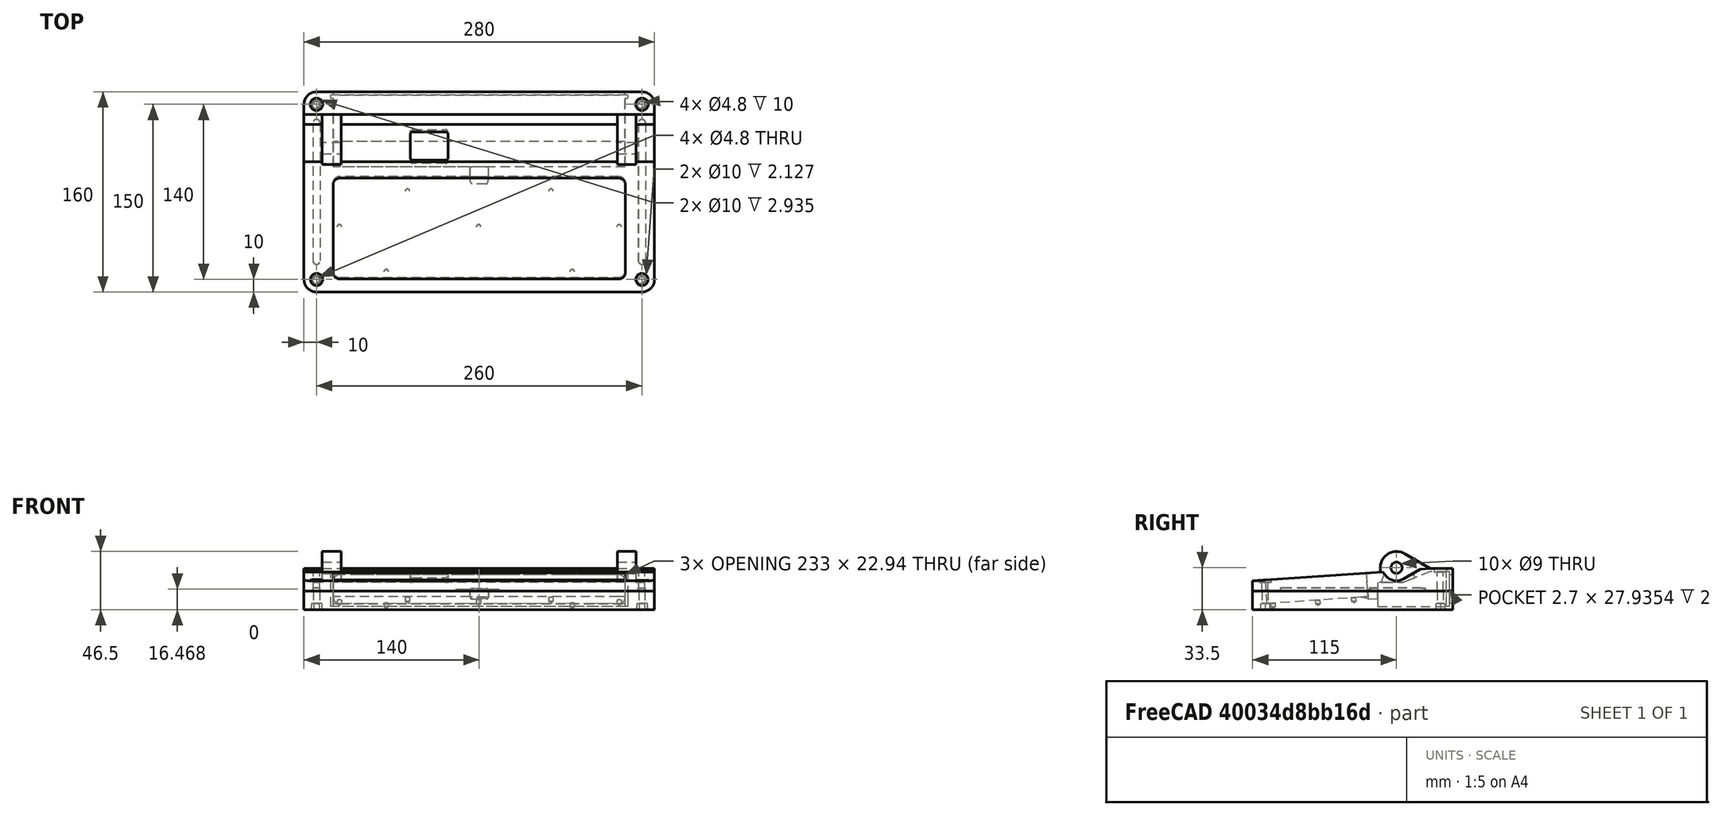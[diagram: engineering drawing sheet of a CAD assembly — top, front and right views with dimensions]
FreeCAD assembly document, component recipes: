
FREECAD ASSEMBLY — COMPONENT RECIPES ("BottomEnclosure_v4")

This assembly document has 8 components, labeled P0..P7 below (a component is one placed body or linked part). 7 of them carry a construction recipe — the FreeCAD feature program that regenerates the part from scratch, quoted from this document or its linked companion documents; the rest are supplied as boundary geometry only. No exploded tour is included for this assembly.
COMPONENT P0 — recipe-attached ("Bottom Enclosure - 1", modeled in this document).
Construction recipe (the document's own serialized feature program — sketch geometry with constraints, then the solid features built on it; lengths are millimeters unless a unit is written):

FEATURE [PartDesign::SubShapeBinder] Binder018
  BindCopyOnChange = 0
  BindMode = 0
  ClaimChildren = false
  Context = -> Body [Binder018.]
  Fuse = false
  MakeFace = false
  OffsetFill = false
  OffsetIntersection = false
  OffsetJoinType = 0
  OffsetOpenResult = false
  PartialLoad = false
  Placement = pos=(2.42e-14,-48.0113,26.6427) rot=(1,0,0;0.069813rad)
  Refine = true
  Relative = true
  Support = -> [Link001,Link002]
  _Version = 2
  expr: .Placement.Rotation.Angle = <<Vars>>.hood_angle
FEATURE [PartDesign::Boolean] Boolean
  Group = -> [Binder019]
  Refine = true
  Suppressed = false
  Type = 0
  UsePlacement = true
FEATURE [PartDesign::SubShapeBinder] Binder020
  BindCopyOnChange = 0
  BindMode = 0
  ClaimChildren = false
  Context = -> Body [Binder020.]
  Fuse = false
  MakeFace = false
  OffsetFill = false
  OffsetIntersection = false
  OffsetJoinType = 0
  OffsetOpenResult = false
  PartialLoad = false
  Placement = pos=(0,0,-19) rot=(0,0,1;0rad)
  Refine = true
  Relative = true
  Support = -> [Binder018]
  _Version = 2
FEATURE [PartDesign::SubShapeBinder] Binder021
  BindCopyOnChange = 0
  BindMode = 0
  ClaimChildren = false
  Context = -> Body [Binder021.]
  Fuse = false
  MakeFace = true
  Offset = 0.2
  OffsetFill = false
  OffsetIntersection = false
  OffsetJoinType = 2
  OffsetOpenResult = false
  PartialLoad = false
  Refine = true
  Relative = true
  Support = -> [Binder020[Edge14,Edge13,Edge7,Edge8,Edge9,Edge10,Edge11,Edge12]]
  _Version = 2
  expr: Offset = <<Vars>>.clearance
FEATURE [PartDesign::Pocket] Pocket005
  BaseFeature = -> Boolean
  Direction = (0,0.0697565,-0.997564)
  Length = 5
  Length2 = 5
  Profile = -> Binder021
  Refine = true
  Reversed = true
  Suppressed = false
  Type = 1
FEATURE [Sketcher::SketchObject] Sketch018  label="Sketch019"
  ArcFitTolerance = 1e-06
  AttachmentSupport = -> [Binder021]
  ExternalGeometry = -> [Pocket005]
  FullyConstrained = true
  MakeInternals = false
  MapMode = 5
  Placement = pos=(0,-0.765452,10.9465) rot=(1,0,0;0.069813rad)
  sketch-geometry (7):
    g0: Circle CenterX=-57.3 CenterY=-18.7812 CenterZ=0 NormalX=0 NormalY=0 NormalZ=1 AngleXU=0 Radius=2.75
    g1: Circle CenterX=-0.5 CenterY=-47.3612 CenterZ=0 NormalX=0 NormalY=0 NormalZ=1 AngleXU=0 Radius=2.75
    g2: Circle CenterX=57.3 CenterY=-18.7812 CenterZ=0 NormalX=0 NormalY=0 NormalZ=1 AngleXU=0 Radius=2.75
    g3: Circle CenterX=111.8 CenterY=-47.3612 CenterZ=0 NormalX=0 NormalY=0 NormalZ=1 AngleXU=0 Radius=2.75
    g4: Circle CenterX=-111.8 CenterY=-47.3612 CenterZ=0 NormalX=0 NormalY=0 NormalZ=1 AngleXU=0 Radius=2.75
    g5: Circle CenterX=-74.3 CenterY=-83.2812 CenterZ=0 NormalX=0 NormalY=0 NormalZ=1 AngleXU=0 Radius=2.75
    g6: Circle CenterX=74.3 CenterY=-83.2812 CenterZ=0 NormalX=0 NormalY=0 NormalZ=1 AngleXU=0 Radius=2.75
  constraints (22):
    c: Equal(g2,g1)
    c: Equal(g1,g0)
    c: Diameter(g1) = 5.5
    c: Equal(g4,g1)
    c: Equal(g1,g3)
    c: Horizontal(g5,g6)
    c: Equal(g6,g5)
    c: Equal(g5,g1)
    c: DistanceY(g5,g0) = 64.5
    c: DistanceX(g5,g0) = 17
    c: DistanceX(g2,g6) = 17
    c: DistanceX(g-3,g4) = 4.9
    c: DistanceY(g4,g-3) = 35.25
    c: DistanceX(g3,g-4) = 4.9
    c: DistanceY(g3,g-4) = 35.25
    c: DistanceX(g-3,g1) = 116.2
    c: DistanceX(g1,g-4) = 117.2
    c: DistanceY(g1,g-3) = 35.25
    c: DistanceX(g2,g-4) = 59.4
    c: DistanceY(g2,g-4) = 6.67
    c: DistanceX(g-3,g0) = 59.4
    c: DistanceY(g0,g-3) = 6.67
FEATURE [PartDesign::SubShapeBinder] Binder023
  BindCopyOnChange = 0
  BindMode = 0
  ClaimChildren = false
  Context = -> Body [Binder023.]
  Fuse = false
  MakeFace = true
  OffsetFill = false
  OffsetIntersection = false
  OffsetJoinType = 0
  OffsetOpenResult = false
  PartialLoad = false
  Refine = true
  Relative = true
  Support = -> [Sketch019]
  _Version = 2
FEATURE [PartDesign::Hole] Hole
  BaseFeature = -> Pocket005
  CustomThreadClearance = 0
  Depth = 3
  DepthType = 0
  Diameter = 3.5
  DrillForDepth = false
  DrillPoint = 1
  DrillPointAngle = 118
  HoleCutCountersinkAngle = 90
  HoleCutCustomValues = false
  HoleCutDepth = 0
  HoleCutDiameter = 6.1
  HoleCutType = 0
  ModelThread = false
  Profile = -> Sketch018
  Refine = true
  Suppressed = false
  Tapered = false
  TaperedAngle = 90
  ThreadClass = 0
  ThreadDepth = 3
  ThreadDepthType = 0
  ThreadDirection = 0
  ThreadFit = 0
  ThreadSize = 0
  ThreadType = 0
  Threaded = false
  UseCustomThreadClearance = false
  expr: Diameter = <<Vars>>.nut_inserts_m2
FEATURE [Sketcher::SketchObject] Sketch019  label="Sketch020"
  ArcFitTolerance = 1e-06
  ExternalGeometry = -> [Hole]
  FullyConstrained = true
  MakeInternals = false
  MapMode = 5
  Placement = pos=(0,-6.89436,-0.482101) rot=(1,0,0;1.64061rad)
  sketch-geometry (12):
    g0: LineSegment StartX=-7.5 StartY=14.9732 StartZ=0 EndX=-7.5 EndY=10.9732 EndZ=0
    g1: LineSegment StartX=-5.5 StartY=8.9732 StartZ=0 EndX=5.5 EndY=8.9732 EndZ=0
    g2: LineSegment StartX=7.5 StartY=10.9732 StartZ=0 EndX=7.5 EndY=14.9732 EndZ=0
    g3: LineSegment StartX=5.5 StartY=16.9732 StartZ=0 EndX=-5.5 EndY=16.9732 EndZ=0
    g4: ArcOfCircle CenterX=-5.5 CenterY=14.9732 CenterZ=0 NormalX=0 NormalY=0 NormalZ=1 AngleXU=0 Radius=2 StartAngle=1.5708 EndAngle=3.14159
    g5: GeomPoint [constr] X=-7.5 Y=16.9732 Z=0
    g6: ArcOfCircle CenterX=5.5 CenterY=14.9732 CenterZ=0 NormalX=0 NormalY=0 NormalZ=1 AngleXU=0 Radius=2 StartAngle=3.45e-14 EndAngle=1.5708
    g7: GeomPoint [constr] X=7.5 Y=16.9732 Z=0
    g8: ArcOfCircle CenterX=-5.5 CenterY=10.9732 CenterZ=0 NormalX=0 NormalY=0 NormalZ=1 AngleXU=0 Radius=2 StartAngle=3.14159 EndAngle=4.71239
    g9: GeomPoint [constr] X=-7.5 Y=8.9732 Z=0
    g10: ArcOfCircle CenterX=5.5 CenterY=10.9732 CenterZ=0 NormalX=0 NormalY=0 NormalZ=1 AngleXU=0 Radius=2 StartAngle=4.71239 EndAngle=6.28319
    g11: GeomPoint [constr] X=7.5 Y=8.9732 Z=0
  constraints (27):
    c: Vertical(g0)
    c: Vertical(g2)
    c: Horizontal(g1)
    c: Symmetric(g5,g7,g-2)
    c: PointOnObject(g5,g0)
    c: PointOnObject(g5,g3)
    c: Tangent(g0,g4) = -1.5708
    c: Tangent(g3,g4) = -1.5708
    c: PointOnObject(g7,g2)
    c: PointOnObject(g7,g3)
    c: Tangent(g2,g6) = -1.5708
    c: Tangent(g3,g6) = -1.5708
    c: Equal(g6,g4)
    c: Radius(g4) = 2
    c: DistanceY(g11,g3) = 8
    c: DistanceX(g0,g2) = 15
    c: PointOnObject(g9,g0)
    c: PointOnObject(g9,g1)
    c: Tangent(g0,g8) = -1.5708
    c: Tangent(g1,g8) = -1.5708
    c: PointOnObject(g11,g1)
    c: PointOnObject(g11,g2)
    c: Tangent(g1,g10) = -1.5708
    c: Tangent(g2,g10) = -1.5708
    c: Equal(g8,g10)
    c: Equal(g10,g6)
    c: DistanceY(g-3,g5) = 6
FEATURE [PartDesign::Pocket] Pocket006
  BaseFeature = -> Hole
  Direction = (0,-0.997564,-0.0697565)
  Length = 5
  Length2 = 5
  Profile = -> Binder023
  Refine = true
  Reversed = true
  Suppressed = false
  Type = 2
FEATURE [PartDesign::SubShapeBinder] Binder054
  BindCopyOnChange = 0
  BindMode = 0
  ClaimChildren = false
  Context = -> Body [Binder054.]
  Fuse = false
  MakeFace = true
  OffsetFill = false
  OffsetIntersection = false
  OffsetJoinType = 0
  OffsetOpenResult = false
  PartialLoad = false
  Refine = true
  Relative = true
  Support = -> [Sketch019]
  _Version = 2
FEATURE [PartDesign::Pocket] Pocket020
  BaseFeature = -> Pocket006
  Direction = (0,-1,0.25)
  Length = 20
  Length2 = 5
  Profile = -> Binder054
  Refine = true
  Suppressed = false
  Type = 0
  UseCustomVector = true
FEATURE [PartDesign::Body] Body  label="Bottom Enclosure - 1"
  AllowCompound = false
  Group = -> [Binder018,Boolean,Binder020,Binder021,Pocket005,Hole,Sketch018,Sketch019,Binder023,Pocket006,Binder054,Pocket020]
  Origin = -> Origin
  Tip = -> Pocket020
COMPONENT P1 — recipe-attached ("Bottom Enclosure - Base", modeled in this document).
Construction recipe (the document's own serialized feature program — sketch geometry with constraints, then the solid features built on it; lengths are millimeters unless a unit is written):

FEATURE [Sketcher::SketchObject] Sketch008
  ArcFitTolerance = 1e-06
  AttachmentSupport = -> [YZ_Plane002]
  FullyConstrained = true
  MakeInternals = false
  MapMode = 5
  Placement = pos=(0,0,0) rot=(0.57735,0.57735,0.57735;2.0944rad)
  expr: Constraints[15] = <<Vars>>.hood_angle
  expr: Constraints[16] = <<Vars>>.bottom_enclosure_height
  expr: Constraints[8] = <<Vars>>.top_enclosure_height
  expr: Constraints[9] = <<Vars>>.bottom_enclosure_depth
  sketch-geometry (12):
    g0: LineSegment StartX=-100 StartY=0 StartZ=0 EndX=-100 EndY=23.0073 EndZ=0
    g1: LineSegment StartX=-100 StartY=23.0073 StartZ=0 EndX=0 EndY=30 EndZ=0
    g2: LineSegment StartX=60 StartY=32.9354 StartZ=0 EndX=60 EndY=0 EndZ=0
    g3: LineSegment StartX=60 StartY=0 StartZ=0 EndX=-100 EndY=0 EndZ=0
    g4: LineSegment [constr] StartX=0 StartY=30 StartZ=0 EndX=-100 EndY=30 EndZ=0
    g5: LineSegment [constr] StartX=-100 StartY=30 StartZ=0 EndX=-100 EndY=23.0073 EndZ=0
    g6: LineSegment [constr] StartX=41.9779 StartY=32.9354 StartZ=0 EndX=21.5 EndY=44.7583 EndZ=0
    g7: LineSegment StartX=0 StartY=30 StartZ=0 EndX=41.9779 EndY=32.9354 EndZ=0
    g8: LineSegment StartX=41.9779 StartY=32.9354 StartZ=0 EndX=60 EndY=32.9354 EndZ=0
    g9: Circle CenterX=15 CenterY=33.5 CenterZ=0 NormalX=0 NormalY=0 NormalZ=1 AngleXU=0 Radius=4.5
    g10: Circle CenterX=15 CenterY=33.5 CenterZ=0 NormalX=0 NormalY=0 NormalZ=1 AngleXU=0 Radius=10
    g11: LineSegment [constr] StartX=15 StartY=33.5 StartZ=0 EndX=21.5 EndY=44.7583 EndZ=0
  constraints (33):
    c: PointOnObject(g0,g-1)
    c: Vertical(g0)
    c: Coincident(g0,g1)
    c: PointOnObject(g1,g-2)
    c: PointOnObject(g2,g-1)
    c: Vertical(g2)
    c: Coincident(g2,g3)
    c: Coincident(g3,g0)
    c: DistanceX(g0,g-1) = 100
    c: DistanceY(g0,g1) = 30
    c: Coincident(g1,g4)
    c: Horizontal(g4)
    c: Coincident(g4,g5)
    c: Coincident(g5,g0)
    c: Vertical(g5)
    c: Angle(g4,g1) = 0.0698132
    c: DistanceX(g0,g2) = 160
    c: Angle(g6,g-1) = 0.523599
    c: Coincident(g7,g1)
    c: Coincident(g7,g6)
    c: Coincident(g8,g6)
    c: Coincident(g8,g2)
    c: Horizontal(g8)
    c: Parallel(g1,g7)
    c: DistanceX(g-1,g9) = 15
    c: Diameter(g9) = 9
    c: DistanceY(g-1,g9) = 33.5
    c: Coincident(g10,g9)
    c: Diameter(g10) = 20
    c: Coincident(g11,g9)
    c: Coincident(g6,g11)
    c: Perpendicular(g6,g11)
    c: Distance(g11) = 13
FEATURE [Sketcher::SketchObject] Sketch
  ArcFitTolerance = 1e-06
  AttachmentSupport = -> [YZ_Plane002]
  ExternalGeometry = -> [Sketch008]
  FullyConstrained = true
  MakeInternals = false
  MapMode = 5
  Placement = pos=(0,0,0) rot=(0.57735,0.57735,0.57735;2.0944rad)
  sketch-geometry (6):
    g0: ArcOfCircle CenterX=15 CenterY=33.5 CenterZ=0 NormalX=0 NormalY=0 NormalZ=1 AngleXU=0 Radius=10.5 StartAngle=3.83972 EndAngle=5.23599
    g1: LineSegment StartX=3.99563 StartY=30.2794 StartZ=0 EndX=6.95653 EndY=26.7507 EndZ=0
    g2: LineSegment StartX=20.25 StartY=24.4067 StartZ=0 EndX=34.0635 EndY=32.382 EndZ=0
    g3: LineSegment [constr] StartX=6.95653 StartY=26.7507 StartZ=0 EndX=7.33956 EndY=27.0721 EndZ=0
    g4: LineSegment [constr] StartX=7.33956 StartY=27.0721 StartZ=0 EndX=15 EndY=33.5 EndZ=0
    g5: LineSegment StartX=3.99563 StartY=30.2794 StartZ=0 EndX=34.0635 EndY=32.382 EndZ=0
  constraints (15):
    c: Coincident(g0,g-3)
    c: PointOnObject(g1,g-5)
    c: Coincident(g3,g1)
    c: Coincident(g4,g0)
    c: PointOnObject(g2,g-5)
    c: Angle(g-1,g2) = 0.523599
    c: Tangent(g0,g1) = -1.5708
    c: Tangent(g0,g2) = -1.5708
    c: Coincident(g3,g4)
    c: PointOnObject(g3,g-4)
    c: Parallel(g3,g4)
    c: Coincident(g5,g1)
    c: Coincident(g5,g2)
    c: Angle(g-1,g4) = 0.698132
    c: Distance(g0,g3) = 0.5
FEATURE [Sketcher::SketchObject] Sketch012  label="Sketch013"
  ArcFitTolerance = 1e-06
  AttachmentSupport = -> [YZ_Plane002]
  ExternalGeometry = -> [Sketch,Sketch008]
  FullyConstrained = true
  MakeInternals = false
  MapMode = 5
  Placement = pos=(0,0,0) rot=(0.57735,0.57735,0.57735;2.0944rad)
  sketch-geometry (7):
    g0: ArcOfCircle CenterX=15 CenterY=33.5 CenterZ=0 NormalX=0 NormalY=0 NormalZ=1 AngleXU=0 Radius=13 StartAngle=1.0472 EndAngle=3.40062
    g1: LineSegment StartX=21.5 StartY=44.7583 StartZ=0 EndX=41.9779 EndY=32.9354 EndZ=0
    g2: LineSegment StartX=2.43368 StartY=30.1702 StartZ=0 EndX=3.99563 EndY=30.2794 EndZ=0
    g3: LineSegment StartX=34.0635 StartY=32.382 StartZ=0 EndX=41.9779 EndY=32.9354 EndZ=0
    g4: LineSegment StartX=3.99563 StartY=30.2794 StartZ=0 EndX=6.95653 EndY=26.7507 EndZ=0
    g5: LineSegment StartX=20.25 StartY=24.4067 StartZ=0 EndX=34.0635 EndY=32.382 EndZ=0
    g6: ArcOfCircle CenterX=15 CenterY=33.5 CenterZ=0 NormalX=0 NormalY=0 NormalZ=1 AngleXU=0 Radius=10.5 StartAngle=3.83972 EndAngle=5.23599
  constraints (16):
    c: Diameter(g0) = 26
    c: Coincident(g0,g-3)
    c: Coincident(g1,g-6)
    c: Tangent(g0,g1) = 1.5708
    c: PointOnObject(g0,g-6)
    c: Coincident(g2,g0)
    c: Coincident(g2,g-4)
    c: Coincident(g3,g-5)
    c: Coincident(g3,g1)
    c: Coincident(g4,g2)
    c: Coincident(g4,g-4)
    c: Coincident(g5,g-5)
    c: Coincident(g5,g3)
    c: Coincident(g6,g4)
    c: Coincident(g6,g5)
    c: Tangent(g6,g-3)
FEATURE [Sketcher::SketchObject] Sketch013  label="Sketch014"
  ArcFitTolerance = 1e-06
  AttachmentSupport = -> [XY_Plane002]
  FullyConstrained = true
  MakeInternals = false
  MapMode = 5
  expr: Constraints[10] = <<Vars>>.wire_hole_offset_x
  expr: Constraints[9] = <<Vars>>.wire_hole_width
  sketch-geometry (5):
    g0: LineSegment StartX=-55 StartY=5 StartZ=0 EndX=-25 EndY=5 EndZ=0
    g1: LineSegment StartX=-25 StartY=5 StartZ=0 EndX=-25 EndY=25 EndZ=0
    g2: LineSegment StartX=-25 StartY=25 StartZ=0 EndX=-55 EndY=25 EndZ=0
    g3: LineSegment StartX=-55 StartY=25 StartZ=0 EndX=-55 EndY=5 EndZ=0
    g4: GeomPoint [constr] X=-40 Y=15 Z=0
  constraints (13):
    c: Coincident(g0,g1)
    c: Coincident(g1,g2)
    c: Coincident(g2,g3)
    c: Coincident(g3,g0)
    c: Horizontal(g0)
    c: Horizontal(g2)
    c: Vertical(g1)
    c: Vertical(g3)
    c: Symmetric(g2,g0,g4)
    c: DistanceX(g2,g2) = 30
    c: DistanceX(g4,g-1) = 40
    c: DistanceY(g-1,g4) = 15
    c: DistanceY(g3,g3) = 20
FEATURE [PartDesign::SubShapeBinder] Binder014
  BindCopyOnChange = 0
  BindMode = 0
  ClaimChildren = false
  Context = -> Body002 [Binder014.]
  Fuse = false
  MakeFace = true
  OffsetFill = false
  OffsetIntersection = false
  OffsetJoinType = 0
  OffsetOpenResult = false
  PartialLoad = false
  Refine = true
  Relative = true
  Support = -> [Sketch008[Edge2,Edge3,Edge4,Edge5,Edge6,Edge1]]
  _Version = 2
FEATURE [PartDesign::Pad] Pad001
  Direction = (1,0,0)
  Length = 280
  Length2 = 10
  Midplane = true
  Profile = -> Binder014
  Refine = true
  Suppressed = false
  Type = 0
  expr: Length = <<Vars>>.top_enclosure_width
FEATURE [Sketcher::SketchObject] Sketch014  label="Sketch015"
  ArcFitTolerance = 1e-06
  AttachmentSupport = -> [YZ_Plane002]
  FullyConstrained = true
  MakeInternals = false
  MapMode = 5
  Placement = pos=(0,0,0) rot=(0.57735,0.57735,0.57735;2.0944rad)
FEATURE [PartDesign::Pocket] Pocket
  BaseFeature = -> Pad001
  Direction = (-1,0,0)
  Length = 5
  Length2 = 5
  Midplane = true
  Profile = -> Sketch
  ReferenceAxis = -> Sketch [N_Axis]
  Refine = true
  Suppressed = false
  Type = 1
FEATURE [PartDesign::SubShapeBinder] Binder
  BindCopyOnChange = 0
  BindMode = 0
  ClaimChildren = false
  Context = -> Body002 [Binder.]
  Fuse = false
  MakeFace = true
  OffsetFill = false
  OffsetIntersection = false
  OffsetJoinType = 0
  OffsetOpenResult = false
  PartialLoad = false
  Placement = pos=(110.4,0,0) rot=(0,0,1;0rad)
  Refine = true
  Relative = true
  Support = -> [Sketch012]
  _Version = 2
  expr: .Placement.Base.x = (<<Vars>>.top_enclosure_width - 32 * 2) / 2 + 2.4
FEATURE [PartDesign::Pad] Pad
  BaseFeature = -> Pocket
  Direction = (1,0,0)
  Length = 15
  Length2 = 10
  Profile = -> Binder
  Refine = true
  Suppressed = false
  Type = 0
FEATURE [PartDesign::Mirrored] Mirrored
  BaseFeature = -> Pad
  MirrorPlane = -> YZ_Plane002
  Originals = -> [Pad]
  Refine = true
  Suppressed = false
  TransformMode = 0
FEATURE [PartDesign::SubShapeBinder] Binder015
  BindCopyOnChange = 0
  BindMode = 0
  ClaimChildren = false
  Context = -> Body002 [Binder015.]
  Fuse = false
  MakeFace = true
  OffsetFill = false
  OffsetIntersection = false
  OffsetJoinType = 0
  OffsetOpenResult = false
  PartialLoad = false
  Refine = true
  Relative = true
  Support = -> [Sketch008[Edge7]]
  _Version = 2
FEATURE [PartDesign::Pocket] Pocket001
  BaseFeature = -> Mirrored
  Direction = (-1,0,0)
  Length = 5
  Length2 = 5
  Midplane = true
  Profile = -> Binder015
  Refine = true
  Suppressed = false
  Type = 1
FEATURE [Sketcher::SketchObject] Sketch015  label="Sketch016"
  ArcFitTolerance = 1e-06
  AttachmentSupport = -> [YZ_Plane002]
  ExternalGeometry = -> [Pocket001]
  FullyConstrained = true
  MakeInternals = false
  MapMode = 5
  Placement = pos=(0,0,0) rot=(0.57735,0.57735,0.57735;2.0944rad)
  expr: Constraints[10] = <<Vars>>.wall
  expr: Constraints[13] = <<Vars>>.wall
  expr: Constraints[17] = <<Vars>>.wall
  expr: Constraints[9] = <<Vars>>.wall
  sketch-geometry (6):
    g0: LineSegment StartX=0 StartY=21.9067 StartZ=0 EndX=0 EndY=2.5 EndZ=0
    g1: LineSegment StartX=0 StartY=2.5 StartZ=0 EndX=57.5 EndY=2.5 EndZ=0
    g2: LineSegment StartX=57.5 StartY=2.5 StartZ=0 EndX=57.5 EndY=30.4354 EndZ=0
    g3: LineSegment StartX=20.25 StartY=21.9067 StartZ=0 EndX=0 EndY=21.9067 EndZ=0
    g4: LineSegment StartX=57.5 StartY=30.4354 StartZ=0 EndX=41.9779 EndY=30.4354 EndZ=0
    g5: LineSegment StartX=41.9779 StartY=30.4354 StartZ=0 EndX=20.25 EndY=21.9067 EndZ=0
  constraints (18):
    c: Coincident(g0,g1)
    c: Coincident(g1,g2)
    c: Coincident(g2,g4)
    c: Coincident(g3,g0)
    c: Vertical(g0)
    c: Vertical(g2)
    c: Horizontal(g1)
    c: Coincident(g5,g3)
    c: Coincident(g4,g5)
    c: DistanceX(g2,g-7) = 2.5
    c: DistanceY(g2,g-7) = 2.5
    c: Horizontal(g4)
    c: PointOnObject(g0,g-2)
    c: DistanceY(g-8,g1) = 2.5
    c: Vertical(g4,g-6)
    c: Vertical(g3,g-5)
    c: Horizontal(g3)
    c: DistanceY(g3,g-5) = 2.5
FEATURE [PartDesign::SubShapeBinder] Binder016
  BindCopyOnChange = 0
  BindMode = 0
  ClaimChildren = false
  Context = -> Body002 [Binder016.]
  Fuse = false
  MakeFace = true
  OffsetFill = false
  OffsetIntersection = false
  OffsetJoinType = 0
  OffsetOpenResult = false
  PartialLoad = false
  Refine = true
  Relative = true
  Support = -> [Sketch015]
  _Version = 2
FEATURE [PartDesign::Pocket] Pocket002
  BaseFeature = -> Pocket001
  Direction = (-1,0,0)
  Length = 233
  Length2 = 5
  Midplane = true
  Profile = -> Binder016
  Refine = true
  Suppressed = false
  Type = 0
  expr: Length = <<Vars>>.keyboard_plate_width
FEATURE [PartDesign::Fillet] Fillet
  Base = -> Pocket002 [Edge25,Edge26,Edge27,Edge33]
  BaseFeature = -> Pocket002
  Radius = 10
  Refine = true
  SupportTransform = false
  Suppressed = false
  UseAllEdges = false
  expr: Radius = <<Vars>>.ext_radius
FEATURE [Sketcher::SketchObject] Sketch016  label="Sketch017"
  ArcFitTolerance = 1e-06
  AttachmentSupport = -> [Fillet]
  ExternalGeometry = -> [Fillet]
  FullyConstrained = true
  MakeInternals = false
  MapMode = 5
  Placement = pos=(0,60,0) rot=(0,0.707107,0.707107;3.14159rad)
  expr: Constraints[27] = <<Vars>>.ext_radius / 2
  expr: Constraints[6] = <<Vars>>.wall
  expr: Constraints[7] = <<Vars>>.wall
  sketch-geometry (12):
    g0: LineSegment StartX=-116.5 StartY=22.9354 StartZ=0 EndX=-116.5 EndY=10 EndZ=0
    g1: LineSegment StartX=-111.5 StartY=5 StartZ=0 EndX=111.5 EndY=5 EndZ=0
    g2: LineSegment StartX=116.5 StartY=10 StartZ=0 EndX=116.5 EndY=22.9354 EndZ=0
    g3: LineSegment StartX=111.5 StartY=27.9354 StartZ=0 EndX=-111.5 EndY=27.9354 EndZ=0
    g4: ArcOfCircle CenterX=111.5 CenterY=22.9354 CenterZ=0 NormalX=0 NormalY=0 NormalZ=1 AngleXU=0 Radius=5 StartAngle=0 EndAngle=1.5708
    g5: GeomPoint [constr] X=116.5 Y=27.9354 Z=0
    g6: ArcOfCircle CenterX=111.5 CenterY=10 CenterZ=0 NormalX=0 NormalY=0 NormalZ=1 AngleXU=0 Radius=5 StartAngle=4.71239 EndAngle=6.28319
    g7: GeomPoint [constr] X=116.5 Y=5 Z=0
    g8: ArcOfCircle CenterX=-111.5 CenterY=22.9354 CenterZ=0 NormalX=0 NormalY=0 NormalZ=1 AngleXU=0 Radius=5 StartAngle=1.5708 EndAngle=3.14159
    g9: GeomPoint [constr] X=-116.5 Y=27.9354 Z=0
    g10: ArcOfCircle CenterX=-111.5 CenterY=10 CenterZ=0 NormalX=0 NormalY=0 NormalZ=1 AngleXU=0 Radius=5 StartAngle=3.14159 EndAngle=4.71239
    g11: GeomPoint [constr] X=-116.5 Y=5 Z=0
  constraints (28):
    c: Vertical(g0)
    c: Vertical(g2)
    c: Horizontal(g1)
    c: Horizontal(g3)
    c: PointOnObject(g9,g-3)
    c: PointOnObject(g7,g-4)
    c: DistanceY(g-4,g7) = 2.5
    c: DistanceY(g5,g-4) = 2.5
    c: PointOnObject(g5,g2)
    c: PointOnObject(g5,g3)
    c: Tangent(g2,g4) = -1.5708
    c: Tangent(g3,g4) = -1.5708
    c: PointOnObject(g7,g1)
    c: PointOnObject(g7,g2)
    c: Tangent(g1,g6) = -1.5708
    c: Tangent(g2,g6) = -1.5708
    c: PointOnObject(g9,g0)
    c: PointOnObject(g9,g3)
    c: Tangent(g0,g8) = -1.5708
    c: Tangent(g3,g8) = -1.5708
    c: PointOnObject(g11,g0)
    c: PointOnObject(g11,g1)
    c: Tangent(g0,g10) = -1.5708
    c: Tangent(g1,g10) = -1.5708
    c: Equal(g6,g4)
    c: Equal(g4,g8)
    c: Equal(g8,g10)
    c: Radius(g10) = 5
FEATURE [PartDesign::Pocket] Pocket003
  BaseFeature = -> Fillet
  Direction = (0,-1,2e-16)
  Length = 5
  Length2 = 5
  Profile = -> Sketch016
  ReferenceAxis = -> Sketch016 [N_Axis]
  Refine = true
  Suppressed = false
  Type = 2
FEATURE [Sketcher::SketchObject] Sketch017  label="Sketch018"
  ArcFitTolerance = 1e-06
  AttachmentSupport = -> [Pocket002]
  ExternalGeometry = -> [Pocket002]
  FullyConstrained = true
  MakeInternals = false
  MapMode = 5
  Placement = pos=(0,60,0) rot=(0,0.707107,0.707107;3.14159rad)
  sketch-geometry (4):
    g0: LineSegment StartX=-118.5 StartY=30.4354 StartZ=0 EndX=-118.5 EndY=2.5 EndZ=0
    g1: LineSegment StartX=-118.5 StartY=2.5 StartZ=0 EndX=118.5 EndY=2.5 EndZ=0
    g2: LineSegment StartX=118.5 StartY=2.5 StartZ=0 EndX=118.5 EndY=30.4354 EndZ=0
    g3: LineSegment StartX=118.5 StartY=30.4354 StartZ=0 EndX=-118.5 EndY=30.4354 EndZ=0
  constraints (12):
    c: Coincident(g0,g1)
    c: Coincident(g1,g2)
    c: Coincident(g2,g3)
    c: Coincident(g3,g0)
    c: Vertical(g0)
    c: Vertical(g2)
    c: Horizontal(g1)
    c: Horizontal(g3)
    c: PointOnObject(g-3,g3)
    c: PointOnObject(g-3,g1)
    c: DistanceX(g-4,g2) = 2
    c: DistanceX(g0,g-3) = 2
FEATURE [PartDesign::SubShapeBinder] Binder017
  BindCopyOnChange = 0
  BindMode = 0
  ClaimChildren = false
  Context = -> Body002 [Binder017.]
  Fuse = false
  MakeFace = true
  OffsetFill = false
  OffsetIntersection = false
  OffsetJoinType = 0
  OffsetOpenResult = false
  PartialLoad = false
  Placement = pos=(0,-2.5,0) rot=(0,0,1;0rad)
  Refine = true
  Relative = true
  Support = -> [Sketch017]
  _Version = 2
  expr: .Placement.Base.y = -<<Vars>>.wall
FEATURE [PartDesign::Pocket] Pocket004
  BaseFeature = -> Pocket003
  Direction = (0,-1,3e-16)
  Length = 2.7
  Length2 = 5
  Profile = -> Binder017
  Refine = true
  Suppressed = false
  Type = 0
  expr: Length = <<Vars>>.wall + <<Vars>>.clearance
FEATURE [PartDesign::Body] Body002  label="Bottom Enclosure - Base"
  AllowCompound = false
  Group = -> [Sketch008,Sketch,Sketch012,Binder014,Pad001,Sketch013,Sketch014,Pocket,Binder,Pad,Mirrored,Binder015,Pocket001,Sketch015,Binder016,Pocket002,Fillet,Sketch016,Pocket003,Sketch017,Binder017,Pocket004]
  Origin = -> Origin002
  Tip = -> Pocket004
COMPONENT P2 — recipe-attached ("Bottom Enclosure - 2", modeled in this document).
Construction recipe (the document's own serialized feature program — sketch geometry with constraints, then the solid features built on it; lengths are millimeters unless a unit is written):

FEATURE [PartDesign::Boolean] Boolean001
  Group = -> [Binder025]
  Refine = true
  Suppressed = false
  Type = 0
  UsePlacement = true
FEATURE [Sketcher::SketchObject] Sketch022  label="Sketch023"
  ArcFitTolerance = 1e-06
  AttachmentSupport = -> [YZ_Plane003]
  ExternalGeometry = -> [Boolean001]
  FullyConstrained = true
  MakeInternals = false
  MapMode = 5
  Placement = pos=(0,0,0) rot=(0.57735,0.57735,0.57735;2.0944rad)
  sketch-geometry (5):
    g0: LineSegment StartX=2 StartY=19.9067 StartZ=0 EndX=7.37275 EndY=33.2121 EndZ=0
    g1: LineSegment StartX=25.5013 StartY=33.2121 StartZ=0 EndX=33.1831 EndY=19.9067 EndZ=0
    g2: LineSegment StartX=33.1831 StartY=19.9067 StartZ=0 EndX=2 EndY=19.9067 EndZ=0
    g3: GeomPoint X=5.47608 Y=28.5151 Z=0
    g4: LineSegment StartX=7.37275 StartY=33.2121 StartZ=0 EndX=25.5013 EndY=33.2121 EndZ=0
  constraints (13):
    c: Perpendicular(g-5,g1)
    c: Distance(g1,g-5) = 5
    c: Distance(g-5,g1) = 7
    c: DistanceY(g1,g-4) = 2
    c: Coincident(g2,g1)
    c: Horizontal(g2)
    c: Coincident(g0,g2)
    c: Horizontal(g0,g1)
    c: DistanceX(g-4,g0) = 2
    c: PointOnObject(g3,g0)
    c: Symmetric(g-6,g-6,g3)
    c: Coincident(g4,g0)
    c: Coincident(g4,g1)
FEATURE [PartDesign::SubShapeBinder] Binder029
  BindCopyOnChange = 0
  BindMode = 0
  ClaimChildren = false
  Context = -> Body003 [Binder029.]
  Fuse = false
  MakeFace = true
  OffsetFill = false
  OffsetIntersection = false
  OffsetJoinType = 0
  OffsetOpenResult = false
  PartialLoad = false
  Placement = pos=(-40,0,0) rot=(0,0,1;0rad)
  Refine = true
  Relative = true
  Support = -> [Sketch022]
  _Version = 2
  expr: .Placement.Base.x = -<<Vars>>.wire_hole_offset_x
FEATURE [PartDesign::Pocket] Pocket008
  BaseFeature = -> Boolean001
  Direction = (-1,0,0)
  Length = 30
  Length2 = 5
  Midplane = true
  Profile = -> Binder029
  Refine = true
  Suppressed = false
  Type = 0
  expr: Length = <<Vars>>.wire_hole_width
FEATURE [PartDesign::Fillet] Fillet001
  Base = -> Pocket008 [Edge53,Edge58,Edge57,Edge63]
  BaseFeature = -> Pocket008
  Radius = 2
  Refine = true
  SupportTransform = false
  Suppressed = false
  UseAllEdges = false
FEATURE [PartDesign::Body] Body003  label="Bottom Enclosure - 2"
  AllowCompound = false
  Group = -> [Boolean001,Sketch022,Binder029,Pocket008,Fillet001]
  Origin = -> Origin003
  Tip = -> Fillet001
COMPONENT P3 — recipe-attached ("Bottom Enclosure - 3", modeled in this document).
Construction recipe (the document's own serialized feature program — sketch geometry with constraints, then the solid features built on it; lengths are millimeters unless a unit is written):

FEATURE [PartDesign::Boolean] Boolean002
  Group = -> [Binder030]
  Refine = true
  Suppressed = false
  Type = 0
  UsePlacement = true
FEATURE [PartDesign::Body] Body005  label="Bottom Enclosure - 3"
  AllowCompound = false
  Group = -> [Boolean002]
  Origin = -> Origin005
  Tip = -> Boolean002
COMPONENT P4 — recipe-attached ("Bottom Enclosure - Bottom - 1", modeled in this document).
Construction recipe (the document's own serialized feature program — sketch geometry with constraints, then the solid features built on it; lengths are millimeters unless a unit is written):

FEATURE [PartDesign::Boolean] Boolean003
  Group = -> [Binder031]
  Refine = true
  Suppressed = false
  Type = 0
  UsePlacement = true
FEATURE [PartDesign::SubShapeBinder] Binder050
  BindCopyOnChange = 0
  BindMode = 0
  ClaimChildren = false
  Context = -> Body006 [Binder050.]
  Fuse = false
  MakeFace = true
  Offset = -0.2
  OffsetFill = false
  OffsetIntersection = false
  OffsetJoinType = 2
  OffsetOpenResult = false
  PartialLoad = false
  Placement = pos=(0,0,15) rot=(0,0,1;0rad)
  Refine = true
  Relative = true
  Support = -> [Sketch028[Edge4,Edge6,Edge5,Edge3]]
  _Version = 2
  expr: .Placement.Base.z = <<LocalVars>>.SplitHeight
  expr: Offset = -<<Vars>>.clearance
FEATURE [PartDesign::SubShapeBinder] Binder051
  BindCopyOnChange = 0
  BindMode = 0
  ClaimChildren = false
  Context = -> Body006 [Binder051.]
  Fuse = false
  MakeFace = true
  OffsetFill = false
  OffsetIntersection = false
  OffsetJoinType = 0
  OffsetOpenResult = false
  PartialLoad = false
  Placement = pos=(0,0,15) rot=(0,0,1;0rad)
  Refine = true
  Relative = true
  Support = -> [Sketch028[Edge2,Edge1]]
  _Version = 2
  expr: .Placement.Base.z = <<LocalVars>>.SplitHeight
FEATURE [PartDesign::Pad] Pad002
  BaseFeature = -> Boolean003
  Direction = (0,0,1)
  Length = 2
  Length2 = 10
  Profile = -> Binder050
  Refine = true
  Suppressed = false
  Type = 0
FEATURE [PartDesign::Hole] Hole007
  BaseFeature = -> Pad002
  CustomThreadClearance = 0
  Depth = 652.335
  DepthType = 1
  Diameter = 4.8
  DrillForDepth = false
  DrillPoint = 1
  DrillPointAngle = 118
  HoleCutCountersinkAngle = 90
  HoleCutCustomValues = false
  HoleCutDepth = 0
  HoleCutDiameter = 6.1
  HoleCutType = 0
  ModelThread = false
  Profile = -> Binder051
  Refine = true
  Suppressed = false
  Tapered = false
  TaperedAngle = 90
  ThreadClass = 0
  ThreadDepth = 652.335
  ThreadDepthType = 0
  ThreadDirection = 0
  ThreadFit = 2
  ThreadSize = 11
  ThreadType = 1
  Threaded = false
  UseCustomThreadClearance = false
FEATURE [Sketcher::SketchObject] Sketch029
  ArcFitTolerance = 1e-06
  AttachmentOffset = pos=(0,0,5) rot=(0,0,1;0rad)
  AttachmentSupport = -> [XY_Plane006]
  ExternalGeometry = -> [Binder051]
  FullyConstrained = true
  MakeInternals = false
  MapMode = 5
  Placement = pos=(0,0,5) rot=(0,0,1;0rad)
  sketch-geometry (14):
    g0: LineSegment StartX=-125.959 StartY=50 StartZ=0 EndX=-127.979 EndY=53.5 EndZ=0
    g1: LineSegment StartX=-127.979 StartY=53.5 StartZ=0 EndX=-132.021 EndY=53.5 EndZ=0
    g2: LineSegment StartX=-132.021 StartY=53.5 StartZ=0 EndX=-134.041 EndY=50 EndZ=0
    g3: LineSegment StartX=-134.041 StartY=50 StartZ=0 EndX=-132.021 EndY=46.5 EndZ=0
    g4: LineSegment StartX=-132.021 StartY=46.5 StartZ=0 EndX=-127.979 EndY=46.5 EndZ=0
    g5: LineSegment StartX=-127.979 StartY=46.5 StartZ=0 EndX=-125.959 EndY=50 EndZ=0
    g6: Circle [constr] CenterX=-130 CenterY=50 CenterZ=0 NormalX=0 NormalY=0 NormalZ=1 AngleXU=0 Radius=4.04145
    g7: LineSegment StartX=-125.959 StartY=-90 StartZ=0 EndX=-127.979 EndY=-86.5 EndZ=0
    g8: LineSegment StartX=-127.979 StartY=-86.5 StartZ=0 EndX=-132.021 EndY=-86.5 EndZ=0
    g9: LineSegment StartX=-132.021 StartY=-86.5 StartZ=0 EndX=-134.041 EndY=-90 EndZ=0
    g10: LineSegment StartX=-134.041 StartY=-90 StartZ=0 EndX=-132.021 EndY=-93.5 EndZ=0
    g11: LineSegment StartX=-132.021 StartY=-93.5 StartZ=0 EndX=-127.979 EndY=-93.5 EndZ=0
    g12: LineSegment StartX=-127.979 StartY=-93.5 StartZ=0 EndX=-125.959 EndY=-90 EndZ=0
    g13: Circle [constr] CenterX=-130 CenterY=-90 CenterZ=0 NormalX=0 NormalY=0 NormalZ=1 AngleXU=0 Radius=4.04145
  constraints (32):
    c: Coincident(g0,g1)
    c: Coincident(g1,g2)
    c: Coincident(g2,g3)
    c: Coincident(g3,g4)
    c: Coincident(g4,g5)
    c: Coincident(g5,g0)
    c: Equal(g0, g1-g5) x5
    c: PointOnObject(g0,g6)
    c: PointOnObject(g1,g6)
    c: PointOnObject(g2,g6)
    c: PointOnObject(g3,g6)
    c: PointOnObject(g4,g6)
    c: PointOnObject(g5,g6)
    c: Coincident(g6,g-3)
    c: Coincident(g7,g8)
    c: Coincident(g8,g9)
    c: Coincident(g9,g10)
    c: Coincident(g10,g11)
    c: Coincident(g11,g12)
    c: Coincident(g12,g7)
    c: Equal(g7, g8-g12) x5
    c: PointOnObject(g7,g13)
    c: PointOnObject(g8,g13)
    c: PointOnObject(g9,g13)
    c: PointOnObject(g10,g13)
    c: PointOnObject(g11,g13)
    c: PointOnObject(g12,g13)
    c: Coincident(g13,g-4)
    c: Horizontal(g8)
    c: Horizontal(g1)
    c: DistanceY(g4,g0) = 7
    c: Equal(g6,g13)
FEATURE [PartDesign::Pocket] Pocket016
  BaseFeature = -> Hole007
  Direction = (0,0,-1)
  Length = 5
  Length2 = 5
  Profile = -> Sketch029
  ReferenceAxis = -> Sketch029 [N_Axis]
  Refine = true
  Suppressed = false
  TaperAngle = 4
  Type = 0
FEATURE [PartDesign::Mirrored] Mirrored007
  BaseFeature = -> Pocket016
  MirrorPlane = -> YZ_Plane006
  Originals = -> [Pad002,Hole007,Pocket016]
  Refine = true
  Suppressed = false
  TransformMode = 0
FEATURE [PartDesign::Body] Body006  label="Bottom Enclosure - Bottom - 1"
  AllowCompound = false
  Group = -> [Boolean003,Binder050,Binder051,Pad002,Hole007,Sketch029,Pocket016,Mirrored007]
  Origin = -> Origin006
  Tip = -> Mirrored007
COMPONENT P5 — recipe-attached ("Bottom Enclosure - Top - 1", modeled in this document).
Construction recipe (the document's own serialized feature program — sketch geometry with constraints, then the solid features built on it; lengths are millimeters unless a unit is written):

FEATURE [PartDesign::Boolean] Boolean004
  Group = -> [Binder034]
  Refine = true
  Suppressed = false
  Type = 0
  UsePlacement = true
FEATURE [PartDesign::SubShapeBinder] Binder052
  BindCopyOnChange = 0
  BindMode = 0
  ClaimChildren = false
  Context = -> Body007 [Binder052.]
  Fuse = false
  MakeFace = true
  OffsetFill = false
  OffsetIntersection = false
  OffsetJoinType = 0
  OffsetOpenResult = false
  PartialLoad = false
  Placement = pos=(0,0,15) rot=(0,0,1;0rad)
  Refine = true
  Relative = true
  Support = -> [Sketch028[Edge4,Edge3,Edge6,Edge5]]
  _Version = 2
  expr: .Placement.Base.z = <<LocalVars>>.SplitHeight
FEATURE [PartDesign::SubShapeBinder] Binder053
  BindCopyOnChange = 0
  BindMode = 0
  ClaimChildren = false
  Context = -> Body007 [Binder053.]
  Fuse = false
  MakeFace = true
  OffsetFill = false
  OffsetIntersection = false
  OffsetJoinType = 0
  OffsetOpenResult = false
  PartialLoad = false
  Placement = pos=(0,0,15) rot=(0,0,1;0rad)
  Refine = true
  Relative = true
  Support = -> [Sketch028[Edge2,Edge1]]
  _Version = 2
  expr: .Placement.Base.z = <<LocalVars>>.SplitHeight
FEATURE [PartDesign::Pocket] Pocket017
  BaseFeature = -> Boolean004
  Direction = (0,0,-1)
  Length = 2.4
  Length2 = 5
  Profile = -> Binder052
  Refine = true
  Reversed = true
  Suppressed = false
  Type = 0
  expr: Length = <<Vars>>.clearance * 2 + 2
FEATURE [PartDesign::Hole] Hole008
  BaseFeature = -> Pocket017
  CustomThreadClearance = 0
  Depth = 654.53
  DepthType = 1
  Diameter = 4.8
  DrillForDepth = false
  DrillPoint = 1
  DrillPointAngle = 118
  HoleCutCountersinkAngle = 90
  HoleCutCustomValues = false
  HoleCutDepth = 0
  HoleCutDiameter = 6.1
  HoleCutType = 0
  ModelThread = false
  Profile = -> Binder053
  Refine = true
  Reversed = true
  Suppressed = false
  Tapered = false
  TaperedAngle = 90
  ThreadClass = 0
  ThreadDepth = 654.53
  ThreadDepthType = 0
  ThreadDirection = 0
  ThreadFit = 2
  ThreadSize = 11
  ThreadType = 1
  Threaded = false
  UseCustomThreadClearance = false
FEATURE [Sketcher::SketchObject] Sketch030
  ArcFitTolerance = 1e-06
  AttachmentOffset = pos=(0,0,30) rot=(0,0,1;0rad)
  AttachmentSupport = -> [XY_Plane007]
  ExternalGeometry = -> [Binder053]
  FullyConstrained = true
  MakeInternals = false
  MapMode = 5
  Placement = pos=(0,0,30) rot=(0,0,1;0rad)
  sketch-geometry (1):
    g0: Circle CenterX=-130 CenterY=50 CenterZ=0 NormalX=0 NormalY=0 NormalZ=1 AngleXU=0 Radius=5
  constraints (2):
    c: Coincident(g0,g-3)
    c: Diameter(g0) = 10
FEATURE [Sketcher::SketchObject] Sketch031
  ArcFitTolerance = 1e-06
  AttachmentOffset = pos=(0,0,22) rot=(0,0,1;0rad)
  AttachmentSupport = -> [XY_Plane007]
  ExternalGeometry = -> [Binder053]
  FullyConstrained = true
  MakeInternals = false
  MapMode = 5
  Placement = pos=(0,0,22) rot=(0,0,1;0rad)
  sketch-geometry (1):
    g0: Circle CenterX=-130 CenterY=-90 CenterZ=0 NormalX=0 NormalY=0 NormalZ=1 AngleXU=0 Radius=5
  constraints (2):
    c: Coincident(g0,g-3)
    c: Diameter(g0) = 10
FEATURE [PartDesign::Pocket] Pocket018
  BaseFeature = -> Hole008
  Direction = (0,0,-1)
  Length = 5
  Length2 = 5
  Profile = -> Sketch030
  ReferenceAxis = -> Sketch030 [N_Axis]
  Refine = true
  Reversed = true
  Suppressed = false
  Type = 1
FEATURE [PartDesign::Pocket] Pocket019
  BaseFeature = -> Pocket018
  Direction = (0,0,-1)
  Length = 5
  Length2 = 5
  Profile = -> Sketch031
  ReferenceAxis = -> Sketch031 [N_Axis]
  Refine = true
  Reversed = true
  Suppressed = false
  Type = 1
FEATURE [PartDesign::Mirrored] Mirrored008
  BaseFeature = -> Pocket019
  MirrorPlane = -> YZ_Plane007
  Originals = -> [Pocket017,Hole008,Pocket018,Pocket019]
  Refine = true
  Suppressed = false
  TransformMode = 0
FEATURE [PartDesign::Body] Body007  label="Bottom Enclosure - Top - 1"
  AllowCompound = false
  Group = -> [Boolean004,Binder052,Binder053,Pocket017,Hole008,Sketch030,Sketch031,Pocket018,Pocket019,Mirrored008]
  Origin = -> Origin007
  Tip = -> Mirrored008
COMPONENT P6 — recipe-attached ("Bottom Enclosure - Bottom - 2", modeled in this document).
Construction recipe (the document's own serialized feature program — sketch geometry with constraints, then the solid features built on it; lengths are millimeters unless a unit is written):

FEATURE [PartDesign::Boolean] Boolean005
  Group = -> [Binder037]
  Refine = true
  Suppressed = false
  Type = 0
  UsePlacement = true
FEATURE [Sketcher::SketchObject] Sketch025  label="RPiZero"
  ArcFitTolerance = 1e-06
  AttachmentSupport = -> [Boolean005]
  FullyConstrained = false
  MakeInternals = false
  MapMode = 5
  Placement = pos=(0,0,2.5) rot=(0,0,1;0rad)
  expr: Constraints[17] = 29 * 2
  sketch-geometry (20):
    g0: LineSegment [constr] StartX=-87.688 StartY=43.0758 StartZ=0 EndX=-87.688 EndY=20.0758 EndZ=0
    g1: LineSegment [constr] StartX=-87.688 StartY=20.0758 StartZ=0 EndX=-29.688 EndY=20.0758 EndZ=0
    g2: LineSegment [constr] StartX=-29.688 StartY=20.0758 StartZ=0 EndX=-29.688 EndY=43.0758 EndZ=0
    g3: LineSegment [constr] StartX=-29.688 StartY=43.0758 StartZ=0 EndX=-87.688 EndY=43.0758 EndZ=0
    g4: Circle CenterX=-87.688 CenterY=43.0758 CenterZ=0 NormalX=0 NormalY=0 NormalZ=1 AngleXU=0 Radius=1.5
    g5: Circle CenterX=-29.688 CenterY=43.0758 CenterZ=0 NormalX=0 NormalY=0 NormalZ=1 AngleXU=0 Radius=1.5
    g6: Circle CenterX=-29.688 CenterY=20.0758 CenterZ=0 NormalX=0 NormalY=0 NormalZ=1 AngleXU=0 Radius=1.5
    g7: Circle CenterX=-87.688 CenterY=20.0758 CenterZ=0 NormalX=0 NormalY=0 NormalZ=1 AngleXU=0 Radius=1.5
    g8: GeomPoint [constr] X=-58.688 Y=31.5758 Z=0
    g9: LineSegment StartX=-87.688 StartY=16.5758 StartZ=0 EndX=-29.688 EndY=16.5758 EndZ=0
    g10: LineSegment StartX=-26.188 StartY=20.0758 StartZ=0 EndX=-26.188 EndY=43.0758 EndZ=0
    g11: LineSegment StartX=-29.688 StartY=46.5758 StartZ=0 EndX=-87.688 EndY=46.5758 EndZ=0
    g12: LineSegment StartX=-91.188 StartY=43.0758 StartZ=0 EndX=-91.188 EndY=20.0758 EndZ=0
    g13: ArcOfCircle CenterX=-87.688 CenterY=20.0758 CenterZ=0 NormalX=0 NormalY=0 NormalZ=1 AngleXU=0 Radius=3.5 StartAngle=3.14159 EndAngle=4.71239
    g14: ArcOfCircle CenterX=-29.688 CenterY=20.0758 CenterZ=0 NormalX=0 NormalY=0 NormalZ=1 AngleXU=0 Radius=3.5 StartAngle=4.71239 EndAngle=6.28319
    g15: ArcOfCircle CenterX=-29.688 CenterY=43.0758 CenterZ=0 NormalX=0 NormalY=0 NormalZ=1 AngleXU=0 Radius=3.5 StartAngle=9e-16 EndAngle=1.5708
    g16: ArcOfCircle CenterX=-87.688 CenterY=43.0758 CenterZ=0 NormalX=0 NormalY=0 NormalZ=1 AngleXU=0 Radius=3.5 StartAngle=1.5708 EndAngle=3.14159
    g17: GeomPoint [constr] X=-26.188 Y=46.5758 Z=0
    g18: GeomPoint [constr] X=-58.688 Y=31.5758 Z=0
    g19: LineSegment [constr] StartX=-58.688 StartY=61.5758 StartZ=0 EndX=-58.688 EndY=1.57578 EndZ=0
  constraints (43):
    c: Coincident(g0,g1)
    c: Coincident(g1,g2)
    c: Coincident(g2,g3)
    c: Coincident(g3,g0)
    c: Vertical(g0)
    c: Vertical(g2)
    c: Horizontal(g1)
    c: Horizontal(g3)
    c: Coincident(g4,g0)
    c: Coincident(g5,g2)
    c: Coincident(g6,g1)
    c: Coincident(g7,g0)
    c: Equal(g7,g4)
    c: Equal(g4,g5)
    c: Equal(g5,g6)
    c: Diameter(g5) = 3
    c: DistanceY(g0,g0) = 23
    c: DistanceX(g3,g3) = 58
    c: Symmetric(g0,g2,g8)
    c: Tangent(g9,g13) = -1.5708
    c: Tangent(g9,g14) = -1.5708
    c: Tangent(g10,g14) = -1.5708
    c: Tangent(g10,g15) = -1.5708
    c: Tangent(g11,g15) = -1.5708
    c: Tangent(g11,g16) = -1.5708
    c: Tangent(g12,g16) = -1.5708
    c: Tangent(g12,g13) = -1.5708
    c: Horizontal(g9)
    c: Horizontal(g11)
    c: Vertical(g10)
    c: Vertical(g12)
    c: Equal(g13,g14)
    c: Equal(g14,g15)
    c: Equal(g15,g16)
    c: Symmetric(g11,g9,g18)
    c: PointOnObject(g17,g10)
    c: PointOnObject(g17,g11)
    c: Distance(g10,g12) = 65
    c: Distance(g9,g11) = 30
    c: Radius(g14) = 3.5
    c: Coincident(g18,g8)
    c: Vertical(g19)
    c: Symmetric(g19,g19,g8)
FEATURE [Sketcher::SketchObject] Sketch026
  ArcFitTolerance = 1e-06
  AttachmentSupport = -> [Boolean005]
  ExternalGeometry = -> [Sketch025]
  FullyConstrained = true
  MakeInternals = false
  MapMode = 5
  Placement = pos=(0,0,2.5) rot=(0,0,1;0rad)
  sketch-geometry (4):
    g0: Circle CenterX=-87.688 CenterY=43.0758 CenterZ=0 NormalX=0 NormalY=0 NormalZ=1 AngleXU=0 Radius=3
    g1: Circle CenterX=-87.688 CenterY=20.0758 CenterZ=0 NormalX=0 NormalY=0 NormalZ=1 AngleXU=0 Radius=3
    g2: Circle CenterX=-29.688 CenterY=20.0758 CenterZ=0 NormalX=0 NormalY=0 NormalZ=1 AngleXU=0 Radius=3
    g3: Circle CenterX=-29.688 CenterY=43.0758 CenterZ=0 NormalX=0 NormalY=0 NormalZ=1 AngleXU=0 Radius=3
  constraints (8):
    c: Coincident(g0,g-4)
    c: Coincident(g1,g-3)
    c: Coincident(g2,g-5)
    c: Coincident(g3,g-6)
    c: Equal(g2,g3)
    c: Equal(g3,g0)
    c: Equal(g0,g1)
    c: Diameter(g1) = 6
FEATURE [PartDesign::Body] Body008  label="Bottom Enclosure - Bottom - 2"
  AllowCompound = false
  Group = -> [Boolean005,Sketch025,Sketch026]
  Origin = -> Origin008
  Tip = -> Boolean005
COMPONENT P7 — geometry summary ("Raspberry Pi Zero 2 W"; no construction recipe available for this part):
  bounding box: 65.8 x 30.6 x 5.1 mm
  tessellated surface: 68,994 triangles
  volume: 3703 mm^3 (36% of its bounding box)
PROVENANCE & LICENSES
A FreeCAD (.FCStd) document from a public repository crawl; recipes are the document's own serialized feature recipes (and, for linked parts, companion documents' recipes).
License: as declared in the source repository (recorded in the dataset sidecar).
